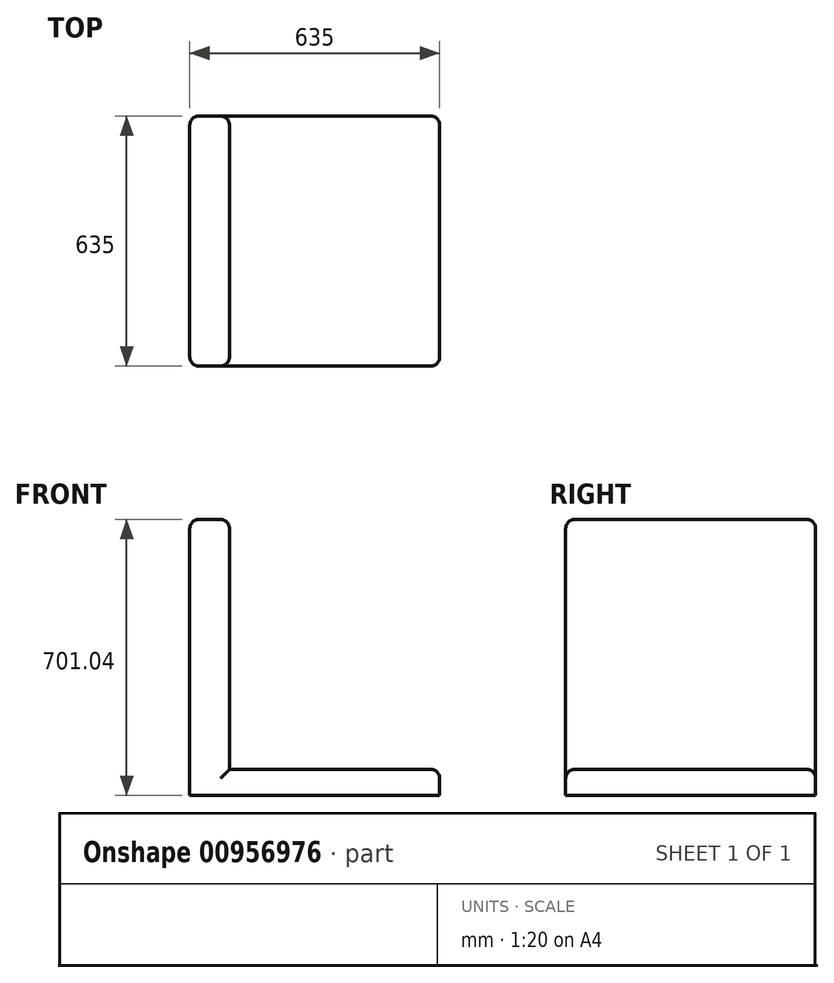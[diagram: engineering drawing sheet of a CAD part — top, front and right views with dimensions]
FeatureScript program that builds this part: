
annotation { "Feature Type Name" : "Feature", "Feature Type Description" : "" }
export const myFeature = defineFeature(function(context is Context, id is Id, definition is map)
    precondition{}
    {
        {
            var Q0;
            Q0=qCreatedBy(makeId("Top.planeOp"),FACE);
            var sketch = newSketch(context, id + "F0", { "sketchPlane" : qUnion([Q0])});
            skLineSegment(sketch, "E0.bottom", {"start": v(-304.46, 333.34) * mm, "end": v(330.54, 333.34) * mm});
            skLineSegment(sketch, "E0.top", {"start": v(-304.46, -301.66) * mm, "end": v(330.54, -301.66) * mm});
            skLineSegment(sketch, "E0.left", {"start": v(-304.46, 333.34) * mm, "end": v(-304.46, -301.66) * mm});
            skLineSegment(sketch, "E0.right", {"start": v(330.54, 333.34) * mm, "end": v(330.54, -301.66) * mm});
            skLineSegment(sketch, "E1.bottom", {"start": v(330.54, -301.66) * mm, "end": v(198.82, -301.66) * mm});
            skLineSegment(sketch, "E1.top", {"start": v(330.54, 333.34) * mm, "end": v(198.82, 333.34) * mm});
            skLineSegment(sketch, "E1.left", {"start": v(330.54, -301.66) * mm, "end": v(330.54, 333.34) * mm});
            skLineSegment(sketch, "E1.right", {"start": v(198.82, -301.66) * mm, "end": v(198.82, 333.34) * mm});
            skSolve(sketch);
        }
        {
            var Q0;
            {var subQ0=sQuery(id+"F0.wireOp",EDGE,"E0.right");var subQ7=sQuery(id+"F0.wireOp",EDGE,"E0.left");Q0=qUnion([makeQuery(id+"F0.imprint","IMPRINT",FACE,{"disambiguationData":[TD([[makeQuery(id+"F0.imprint","IMPRINT",EDGE,{"derivedFrom":subQ7}),1.0]])]}),makeQuery(id+"F0.imprint","IMPRINT",FACE,{"disambiguationData":[TD([[makeQuery(id+"F0.imprint","IMPRINT",EDGE,{"derivedFrom":subQ0}),-1.0]])]})]);}
            extrude(context, id + "F1", {"entities" : qUnion([Q0]), "depth" : 66.04 * mm, "offsetDistance" : 25.4 * mm});
        }
        {
            var Q0;
            Q0=makeQuery(id+"F1.opExtrude","CAP_FACE",FACE,{"disambiguationData":[OSD([sQuery(id+"F0.wireOp",EDGE,"E0.bottom"),sQuery(id+"F0.wireOp",EDGE,"E0.top"),sQuery(id+"F0.wireOp",EDGE,"E0.left"),sQuery(id+"F0.wireOp",EDGE,"E0.right")])],"isStart":false});
            var sketch = newSketch(context, id + "F2", { "sketchPlane" : qUnion([Q0])});
            skLineSegment(sketch, "E2.bottom", {"start": v(-304.46, -301.66) * mm, "end": v(-203.77, -301.66) * mm});
            skLineSegment(sketch, "E2.top", {"start": v(-304.46, 333.34) * mm, "end": v(-203.77, 333.34) * mm});
            skLineSegment(sketch, "E2.left", {"start": v(-304.46, -301.66) * mm, "end": v(-304.46, 333.34) * mm});
            skLineSegment(sketch, "E2.right", {"start": v(-203.77, -301.66) * mm, "end": v(-203.77, 333.34) * mm});
            skSolve(sketch);
        }
        {
            var Q0;
            Q0 = qSketchRegion(id + "F2", true);
            extrude(context, id + "F3", {"entities" : qUnion([Q0]), "operationType" : NewBodyOperationType.ADD, "depth" : 635 * mm, "offsetDistance" : 25.4 * mm});
        }
        {
            var Q0;
            Q0=makeQuery(id+"F3.opExtrude","CAP_EDGE",EDGE,{"disambiguationData":[OSD([sQuery(id+"F2.wireOp",EDGE,"E2.right")])],"isStart":false});
            var Q1;
            Q1=makeQuery(id+"F3.opExtrude","CAP_EDGE",EDGE,{"disambiguationData":[OSD([sQuery(id+"F2.wireOp",EDGE,"E2.left")])],"isStart":false});
            fillet(context, id + "F4", {"entities" : qUnion([Q0, Q1]), "radius" : 22.86 * mm, "tangentPropagation" : true, "allowEdgeOverflow" : false});
        }
        {
            var Q0;
            Q0=makeQuery(id+"F3.opExtrude","SWEPT_EDGE",EDGE,{"disambiguationData":[OSD([sQuery(id+"F0.wireOp",EDGE,"E0.top"),sQuery(id+"F2.wireOp",EDGE,"E2.bottom"),sQuery(id+"F2.wireOp",EDGE,"E2.right")])]});
            var Q1;
            Q1=makeQuery(id+"F1.opExtrude","CAP_EDGE",EDGE,{"disambiguationData":[OSD([sQuery(id+"F0.wireOp",EDGE,"E0.top")])],"isStart":false});
            var Q2;
            Q2=makeQuery(id+"F1.opExtrude","CAP_EDGE",EDGE,{"disambiguationData":[OSD([sQuery(id+"F0.wireOp",EDGE,"E0.right")])],"isStart":false});
            var Q3;
            Q3=makeQuery(id+"F1.opExtrude","CAP_EDGE",EDGE,{"disambiguationData":[OSD([sQuery(id+"F0.wireOp",EDGE,"E0.bottom")])],"isStart":false});
            fillet(context, id + "F5", {"entities" : qUnion([Q0, Q1, Q2, Q3]), "radius" : 22.86 * mm, "tangentPropagation" : true, "allowEdgeOverflow" : false});
        }
        {
            var Q0;
            Q0=makeQuery(id+"F3.opExtrude","SWEPT_EDGE",EDGE,{"disambiguationData":[OSD([sQuery(id+"F0.wireOp",EDGE,"E0.bottom"),sQuery(id+"F2.wireOp",EDGE,"E2.top"),sQuery(id+"F2.wireOp",EDGE,"E2.right")])]});
            var Q1;
            Q1=makeQuery(id+"F3.boolean.opBoolean","MERGE",EDGE,{"derivedFrom":[makeQuery(id+"F1.opExtrude","SWEPT_EDGE",EDGE,{"disambiguationData":[OSD([sQuery(id+"F0.wireOp",EDGE,"E0.bottom"),sQuery(id+"F0.wireOp",EDGE,"E0.left")])]}),makeQuery(id+"F3.opExtrude","SWEPT_EDGE",EDGE,{"disambiguationData":[OSD([sQuery(id+"F2.wireOp",EDGE,"E2.top"),sQuery(id+"F2.wireOp",EDGE,"E2.left")])]})]});
            fillet(context, id + "F6", {"entities" : qUnion([Q0, Q1]), "radius" : 22.86 * mm, "tangentPropagation" : true, "allowEdgeOverflow" : false});
        }
        {
            var Q0;
            Q0=makeQuery(id+"F1.opExtrude","SWEPT_EDGE",EDGE,{"disambiguationData":[OSD([sQuery(id+"F0.wireOp",EDGE,"E0.bottom"),sQuery(id+"F0.wireOp",EDGE,"E0.right")])]});
            var Q1;
            Q1=makeQuery(id+"F1.opExtrude","SWEPT_EDGE",EDGE,{"disambiguationData":[OSD([sQuery(id+"F0.wireOp",EDGE,"E0.top"),sQuery(id+"F0.wireOp",EDGE,"E0.right")])]});
            fillet(context, id + "F7", {"entities" : qUnion([Q0, Q1]), "radius" : 22.86 * mm, "tangentPropagation" : true, "allowEdgeOverflow" : false});
        }
    });
